# Revit family: Lighting_Pendants_Radian_Recessed-Pline-module-isolated
name_source: partatom
category: Luminaires
revit_build: Autodesk Revit Architecture 2016 (Build: 20150220_1215(x64)
units: mm (PartAtom-declared; Revit-internal decimal feet)

## family parameters
Basée sur le plan de construction = Non
Cote de connecteur circulaire = Utiliser le diamètre
Couper avec des vides une fois chargée = Non
Numéro OmniClass = 23.80.70.00
Partagée = Non
Point de calcul de pièce = Non
Source d'éclairage = Oui
Titre OmniClass = Lighting
Toujours verticalement = Non
Type d'élément = Normal

## types (14) — shared parameters
Angle de l'inclinaison = 90.00°
BIMobject category = Pendants
BIMobject category code = lighting-pendants
BIMobject main category = Lighting
BIMobject main category code = lighting
BOSUseNativeGeometries = 1
Brand url = http://www.radian.fr
Design country = France
Edition number = 1
Emettre la visibilité des formes dans le rendu = Oui
Emettre à partir de la largeur du rectangle = 74 mm  [stored 0.242782 ft]
Filtre de couleur = 16777215
Gradation des changements de température de couleur de lampe = <Aucun>
IFC Classification = Light Fixture
Manufacturer country = France
Manufacturer name = Radian
Masterformat 2014 Code = 26 50 00
Masterformat 2014 Description = Lighting
Material main = Aluminium
NBS Reference Code = 70-80
NBS Reference Description = Lighting Systems
OmniClass Code = 23-35 47 00
OmniClass Description = Electrical Lighting
Product Guid = 1304d3d7-f58f-49ea-9d61-4cade5f400fa
Product SKU = pline-enc
Product data url = https://bimobject.com
Product family = Lighting
Product group = Pline
Product name = Recessed Pline module isolated
QR code = http://bimobject.com
Radian-Adresse = 5ter rue d'Arsonval - 75015 Paris - France
Radian-Fabricant = Radian
Radian-Fax = 0033 (0)1 43 21 72 61
Radian-Telephone = 0033 (0)1 43 21 65 65
Radian-URL = http://www.radian.fr
UNSPSC Code = 391016
Uniclass 1.4 Code = JV5
Uniclass 1.4 Description = General lighting
Uniclass 2.0 Code = SS-70-80
Uniclass 2.0 Description = Lighting Systems
Uniclass 2015 Code = Ss_70_80
Uniclass 2015 Name = Lighting systems
Uniformat II Code = D5020
Uniformat II Description = Lighting & Branch Wiring

## per-type parameters (varying)
| type | Emettre à partir de la longueur du rectangle | Fichier de distribution photométrique | Separate Electrical Box |
| TYPE - (Ref 342  Encastre Pline module isole Lg 1125mm - 17w)  Colour - (RAL9003) | 1119 mm | RADIAN PLINE 17W.ies | 1 |
| TYPE - (Ref 342  Encastre Pline module isole Lg 1125mm - 17w)  Colour - (RAL7047) | 1119 mm | RADIAN PLINE 17W.ies | 1 |
| TYPE - (Ref 344 Encastre Pline module isole Lg 1685mm - 25W)  Colour - (RAL9003) | 1679 mm  [stored 5.50853 ft] | RADIAN PLINE 25W.ies | 0 |
| TYPE - (Ref 344 Encastre Pline module isole Lg 1685mm - 25W)  Colour - (RAL7047) | 1679 mm  [stored 5.50853 ft] | RADIAN PLINE 25W.ies | 0 |
| TYPE - (Ref 346 Encastre Pline module isole Lg 2245mm - 33W)  Colour - (RAL9003) | 2239 mm  [stored 7.3458 ft] | RADIAN PLINE 33W.ies | 0 |
| TYPE - (Ref 346 Encastre Pline module isole Lg 2245mm - 33W)  Colour - (RAL7047) | 2239 mm  [stored 7.3458 ft] | RADIAN PLINE 33W.ies | 0 |
| TYPE - (Ref 348 Encastre Pline module isole Lg 2805mm - 41W)  Colour - (RAL9003) | 2799 mm | RADIAN PLINE 41W.ies | 0 |
| TYPE - (Ref 348 Encastre Pline module isole Lg 2805mm - 41W)  Colour - (RAL7047) | 2799 mm | RADIAN PLINE 41W.ies | 0 |
| TYPE - (Ref 355 Encastre Pline module isole Lg 565mm - 8W)  Colour - (RAL9003) | 274 mm  [stored 0.89895 ft] | RADIAN PLINE 8W.ies | 1 |
| TYPE - (Ref 355 Encastre Pline module isole Lg 565mm - 8W)  Colour - (RAL7047) | 274 mm  [stored 0.89895 ft] | RADIAN PLINE 8W.ies | 1 |
| TYPE - (Ref 356 Encastre Pline module isole Lg 1405mm - 21W)  Colour - (RAL9003) | 559 mm | RADIAN PLINE 21W.ies | 1 |
| TYPE - (Ref 356 Encastre Pline module isole Lg 1405mm - 21W)  Colour - (RAL7047) | 559 mm | RADIAN PLINE 21W.ies | 1 |
| TYPE - (Ref 354 Encastre Pline module isole Lg 285mm  - 4W)  Colour - (RAL9003) | 1399 mm | RADIAN PLINE 4W.ies | 0 |
| TYPE - (Ref 354 Encastre Pline module isole Lg 285mm  - 4W)  Colour - (RAL7047) | 1399 mm | RADIAN PLINE 4W.ies | 0 |

note: [stored X ft] marks values corroborated as IEEE doubles in the binary element streams (Revit-internal decimal feet)

## geometry (parser evidence)
native form markers: Sweep x4
no freeform markers — native parametric forms only
